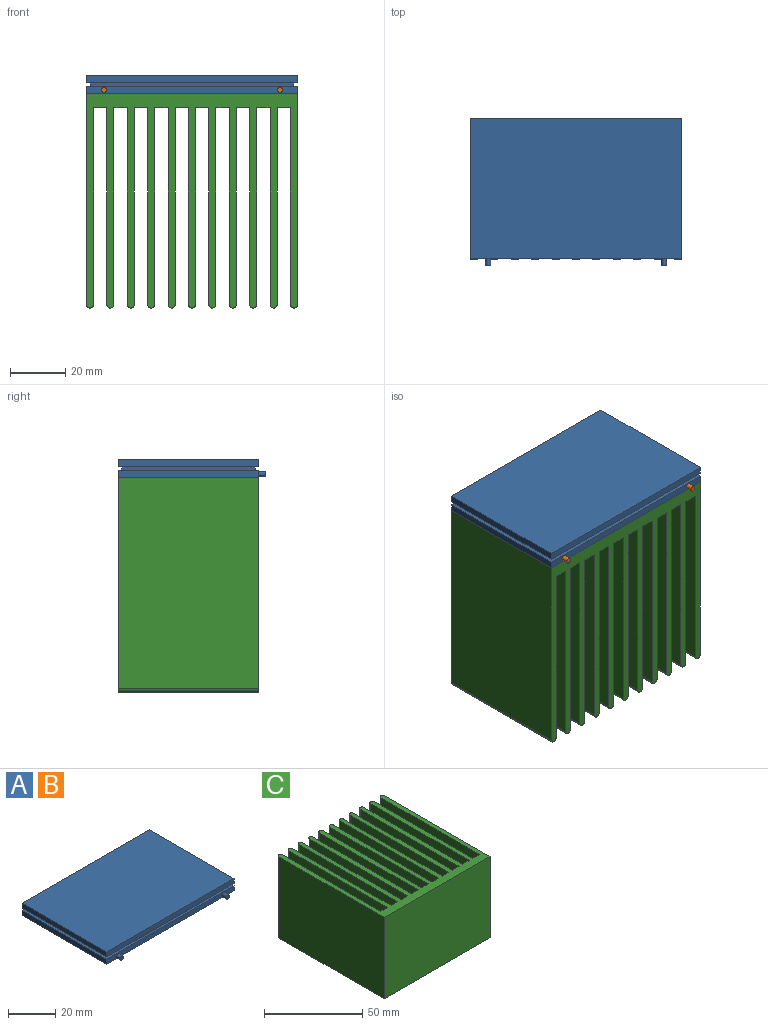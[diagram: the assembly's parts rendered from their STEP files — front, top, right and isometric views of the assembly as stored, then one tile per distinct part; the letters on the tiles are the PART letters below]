
ASSEMBLY  parts=3 mates=1
PART A: 20 faces, bbox 76.2x53.3x6.4 mm
  f0: plane 76.2x50.8mm, normal (0,0,1), area 316.1mm2, adj f1,f2,f3,f4,f6,f7,f8,f9
  f1: plane 50.8x2.54mm, normal (1,0,0), area 129mm2, adj f0,f2,f4,f5
  f2: plane 76.2x2.54mm, normal (0,1,0), area 193.5mm2, adj f0,f1,f3,f5
  f3: plane 50.8x2.54mm, normal (-1,0,0), area 129mm2, adj f0,f2,f4,f5
  f4: plane 76.2x2.54mm, normal (0,-1,0), area 187.8mm2, adj f0,f1,f3,f5,f16,f18
  f5: plane 76.2x50.8mm, normal (0,0,-1), area 3871mm2, adj f1,f2,f3,f4
  f6: plane 73.66x1.27mm, normal (0,-1,0), area 93.5mm2, adj f0,f7,f9,f10
  f7: plane 48.26x1.27mm, normal (1,0,0), area 61.3mm2, adj f0,f6,f8,f10
  f8: plane 73.66x1.27mm, normal (0,1,0), area 93.5mm2, adj f0,f7,f9,f10
  f9: plane 48.26x1.27mm, normal (-1,0,0), area 61.3mm2, adj f0,f6,f8,f10
  f10: plane 76.2x50.8mm, normal (0,0,-1), area 316.1mm2, adj f6,f7,f8,f9,f11,f12,f13,f14
  f11: plane 50.8x2.54mm, normal (1,0,0), area 129mm2, adj f10,f12,f14,f15
  f12: plane 76.2x2.54mm, normal (0,1,0), area 193.5mm2, adj f10,f11,f13,f15
  f13: plane 50.8x2.54mm, normal (-1,0,0), area 129mm2, adj f10,f12,f14,f15
  f14: plane 76.2x2.54mm, normal (0,-1,0), area 193.5mm2, adj f10,f11,f13,f15
  f15: plane 76.2x50.8mm, normal (0,0,1), area 3871mm2, adj f11,f12,f13,f14
  f16: cylinder r=0.95mm len=2.54mm, axis (0,1,0), area 15.2mm2, adj f4,f17
  f17: plane 1.91x1.91mm, normal (0,-1,0), area 2.9mm2, adj f16
  f18: cylinder r=0.95mm len=2.54mm, axis (0,1,0), area 15.2mm2, adj f4,f19
  f19: plane 1.91x1.91mm, normal (0,-1,0), area 2.9mm2, adj f18
PART B: same geometry as A
PART C: 46 faces, bbox 76.2x77.5x50.8 mm
  f0: cylinder r=1.27mm len=50.8mm, axis (0,0,-1), area 202.7mm2, adj f1,f43,f44,f45
  f1: plane 76.2x50.8mm, normal (-1,0,0), area 3871mm2, adj f0,f2,f44,f45
  f2: plane 76.2x50.8mm, normal (0,-1,0), area 3871mm2, adj f1,f3,f44,f45
  f3: plane 76.2x50.8mm, normal (1,0,0), area 3871mm2, adj f2,f4,f44,f45
  f4: cylinder r=1.27mm len=50.8mm, axis (0,0,-1), area 202.7mm2, adj f3,f5,f44,f45
  f5: plane 71.12x50.8mm, normal (-1,0,0), area 3612.9mm2, adj f4,f6,f44,f45
  f6: plane 50.8x4.83mm, normal (0,1,0), area 245.2mm2, adj f5,f7,f44,f45
  f7: plane 71.12x50.8mm, normal (1,0,0), area 3612.9mm2, adj f6,f8,f44,f45
  f8: cylinder r=1.27mm len=50.8mm, axis (0,0,-1), area 202.7mm2, adj f7,f9,f44,f45
  f9: plane 71.12x50.8mm, normal (-1,0,0), area 3612.9mm2, adj f8,f10,f44,f45
  f10: plane 50.8x4.83mm, normal (0,1,0), area 245.2mm2, adj f9,f11,f44,f45
  f11: plane 71.12x50.8mm, normal (1,0,0), area 3612.9mm2, adj f10,f12,f44,f45
  f12: cylinder r=1.27mm len=50.8mm, axis (0,0,-1), area 202.7mm2, adj f11,f13,f44,f45
  f13: plane 71.12x50.8mm, normal (-1,0,0), area 3612.9mm2, adj f12,f14,f44,f45
  f14: plane 50.8x4.83mm, normal (0,1,0), area 245.2mm2, adj f13,f15,f44,f45
  f15: plane 71.12x50.8mm, normal (1,0,0), area 3612.9mm2, adj f14,f16,f44,f45
  f16: cylinder r=1.27mm len=50.8mm, axis (0,0,-1), area 202.7mm2, adj f15,f17,f44,f45
  f17: plane 71.12x50.8mm, normal (-1,0,0), area 3612.9mm2, adj f16,f18,f44,f45
  f18: plane 50.8x4.83mm, normal (0,1,0), area 245.2mm2, adj f17,f19,f44,f45
  f19: plane 71.12x50.8mm, normal (1,0,0), area 3612.9mm2, adj f18,f20,f44,f45
  f20: cylinder r=1.27mm len=50.8mm, axis (0,0,-1), area 202.7mm2, adj f19,f21,f44,f45
  f21: plane 71.12x50.8mm, normal (-1,0,0), area 3612.9mm2, adj f20,f22,f44,f45
  f22: plane 50.8x4.83mm, normal (0,1,0), area 245.2mm2, adj f21,f23,f44,f45
  f23: plane 71.12x50.8mm, normal (1,0,0), area 3612.9mm2, adj f22,f24,f44,f45
  f24: cylinder r=1.27mm len=50.8mm, axis (0,0,-1), area 202.7mm2, adj f23,f25,f44,f45
  f25: plane 71.12x50.8mm, normal (-1,0,0), area 3612.9mm2, adj f24,f26,f44,f45
  f26: plane 50.8x4.83mm, normal (0,1,0), area 245.2mm2, adj f25,f27,f44,f45
  f27: plane 71.12x50.8mm, normal (1,0,0), area 3612.9mm2, adj f26,f28,f44,f45
  f28: cylinder r=1.27mm len=50.8mm, axis (0,0,-1), area 202.7mm2, adj f27,f29,f44,f45
  f29: plane 71.12x50.8mm, normal (-1,0,0), area 3612.9mm2, adj f28,f30,f44,f45
  f30: plane 50.8x4.83mm, normal (0,1,0), area 245.2mm2, adj f29,f31,f44,f45
  f31: plane 71.12x50.8mm, normal (1,0,0), area 3612.9mm2, adj f30,f32,f44,f45
  f32: cylinder r=1.27mm len=50.8mm, axis (0,0,-1), area 202.7mm2, adj f31,f33,f44,f45
  f33: plane 71.12x50.8mm, normal (-1,0,0), area 3612.9mm2, adj f32,f34,f44,f45
  f34: plane 50.8x4.83mm, normal (0,1,0), area 245.2mm2, adj f33,f35,f44,f45
  f35: plane 71.12x50.8mm, normal (1,0,0), area 3612.9mm2, adj f34,f36,f44,f45
  f36: cylinder r=1.27mm len=50.8mm, axis (0,0,-1), area 202.7mm2, adj f35,f37,f44,f45
  f37: plane 71.12x50.8mm, normal (-1,0,0), area 3612.9mm2, adj f36,f38,f44,f45
  f38: plane 50.8x4.83mm, normal (0,1,0), area 245.2mm2, adj f37,f39,f44,f45
  f39: plane 71.12x50.8mm, normal (1,0,0), area 3612.9mm2, adj f38,f40,f44,f45
  f40: cylinder r=1.27mm len=50.8mm, axis (0,0,-1), area 202.7mm2, adj f39,f41,f44,f45
  f41: plane 71.12x50.8mm, normal (-1,0,0), area 3612.9mm2, adj f40,f42,f44,f45
  f42: plane 50.8x4.83mm, normal (0,1,0), area 245.2mm2, adj f41,f43,f44,f45
  f43: plane 71.12x50.8mm, normal (1,0,0), area 3612.9mm2, adj f0,f42,f44,f45
  f44: plane 77.47x76.2mm, normal (0,0,1), area 2402.1mm2, adj f0,f1,f2,f3,f4,f5,f6,f7
  f45: plane 77.47x76.2mm, normal (0,0,-1), area 2402.1mm2, adj f0,f1,f2,f3,f4,f5,f6,f7
PLACE A at identity
PLACE B at identity
PLACE C rot(axis=(-1,0,0),90deg) t=(0,0,-38.1)mm
MATE fastened C.f2 <-> B.f5  axis (0,0,1) through (0,0,0)mm
